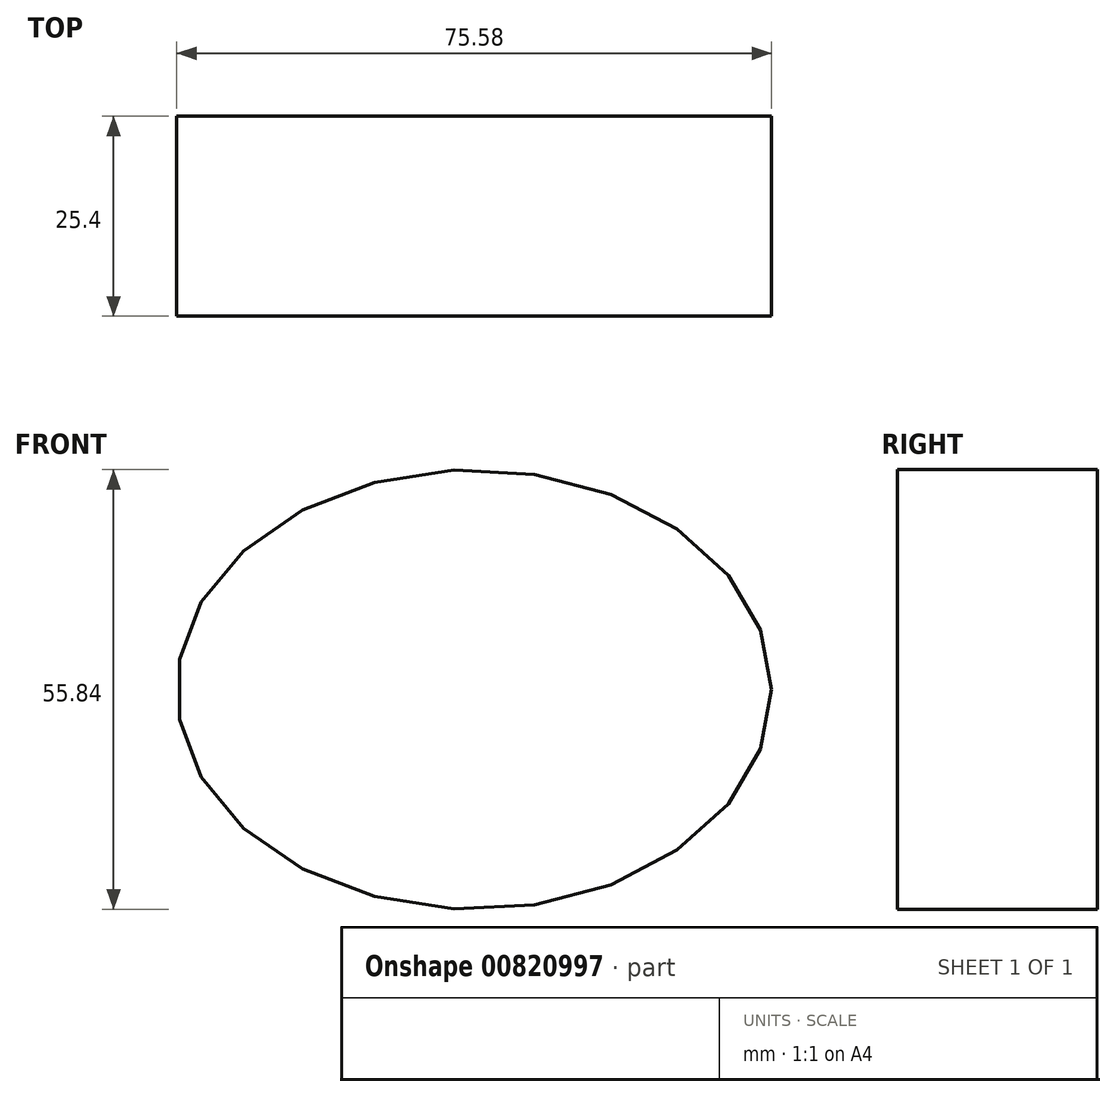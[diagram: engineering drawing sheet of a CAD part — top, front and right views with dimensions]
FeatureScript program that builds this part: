
annotation { "Feature Type Name" : "Feature", "Feature Type Description" : "" }
export const myFeature = defineFeature(function(context is Context, id is Id, definition is map)
    precondition{}
    {
        {
            var Q0;
            Q0=qCreatedBy(makeId("Front.planeOp"),FACE);
            var sketch = newSketch(context, id + "F0", { "sketchPlane" : qUnion([Q0])});
            skEllipse(sketch, "E0", {"center": v(0, 0) * mm, "majorRadius": 37.79 * mm, "minorRadius": 27.92 * mm, "majorAxis": v(1, 0)});
            skSolve(sketch);
        }
        {
            var Q0;
            Q0=makeQuery(id+"F0.imprint","IMPRINT",FACE,{"disambiguationData":[TD([[makeQuery(id+"F0.imprint","IMPRINT",EDGE,{"derivedFrom":sQuery(id+"F0.wireOp",EDGE,"E0")}),1.0]])]});
            var sketch = newSketch(context, id + "F1", { "sketchPlane" : qUnion([Q0])});
            skLineSegment(sketch, "E1", {"start": v(0, -14.2) * mm, "end": v(0, 13.97) * mm});
            skSolve(sketch);
        }
        {
            var Q0;
            Q0=makeQuery(id+"F0.imprint","IMPRINT",FACE,{"disambiguationData":[TD([[makeQuery(id+"F0.imprint","IMPRINT",EDGE,{"derivedFrom":sQuery(id+"F0.wireOp",EDGE,"E0")}),1.0]])]});
            var sketch = newSketch(context, id + "F2", { "sketchPlane" : qUnion([Q0])});
            skCircle(sketch, "E2", {"center": v(0, 0) * mm, "radius": 5.33 * mm});
            skSolve(sketch);
        }
        {
            var Q0;
            Q0=makeQuery(id+"F0.imprint","IMPRINT",FACE,{"disambiguationData":[TD([[makeQuery(id+"F0.imprint","IMPRINT",EDGE,{"derivedFrom":sQuery(id+"F0.wireOp",EDGE,"E0")}),1.0]])]});
            extrude(context, id + "F3", {"entities" : qUnion([Q0]), "depth" : 25.4 * mm, "offsetDistance" : 25.4 * mm});
        }
        {
            var Q0;
            Q0=makeQuery(id+"F2.imprint","IMPRINT",FACE,{"disambiguationData":[TD([[makeQuery(id+"F2.imprint","IMPRINT",EDGE,{"derivedFrom":sQuery(id+"F2.wireOp",EDGE,"E2")}),1.0]])]});
            extrude(context, id + "F4", {"entities" : qUnion([Q0]), "operationType" : NewBodyOperationType.REMOVE, "oppositeDirection" : true, "depth" : 25.4 * mm, "offsetDistance" : 25.4 * mm});
        }
        {
            var Q0;
            Q0=makeQuery(id+"F1.imprint","IMPRINT",FACE,{"disambiguationData":[TD([[makeQuery(id+"F1.imprint","IMPRINT",EDGE,{"derivedFrom":makeQuery(id+"F0.imprint","IMPRINT",EDGE,{"derivedFrom":sQuery(id+"F0.wireOp",EDGE,"E0")})}),1.0]])]});
            var sketch = newSketch(context, id + "F5", { "sketchPlane" : qUnion([Q0])});
            skArc(sketch, "E3", {"start": v(0, 14.06) * mm, "mid": v(-14, -0.02) * mm, "end": v(0, -14.1) * mm});
            skSolve(sketch);
        }
        {
            var Q0;
            Q0=sQuery(id+"F5.wireOp",EDGE,"E3");
            var Q1;
            Q1=sQuery(id+"F1.wireOp",EDGE,"E1");
            revolve(context, id + "F6", {"bodyType" : ToolBodyType.SURFACE, "surfaceOperationType" : NewSurfaceOperationType.NEW, "surfaceEntities" : qUnion([Q0]), "axis" : qUnion([Q1]), "revolveType" : RevolveType.FULL});
        }
    });
